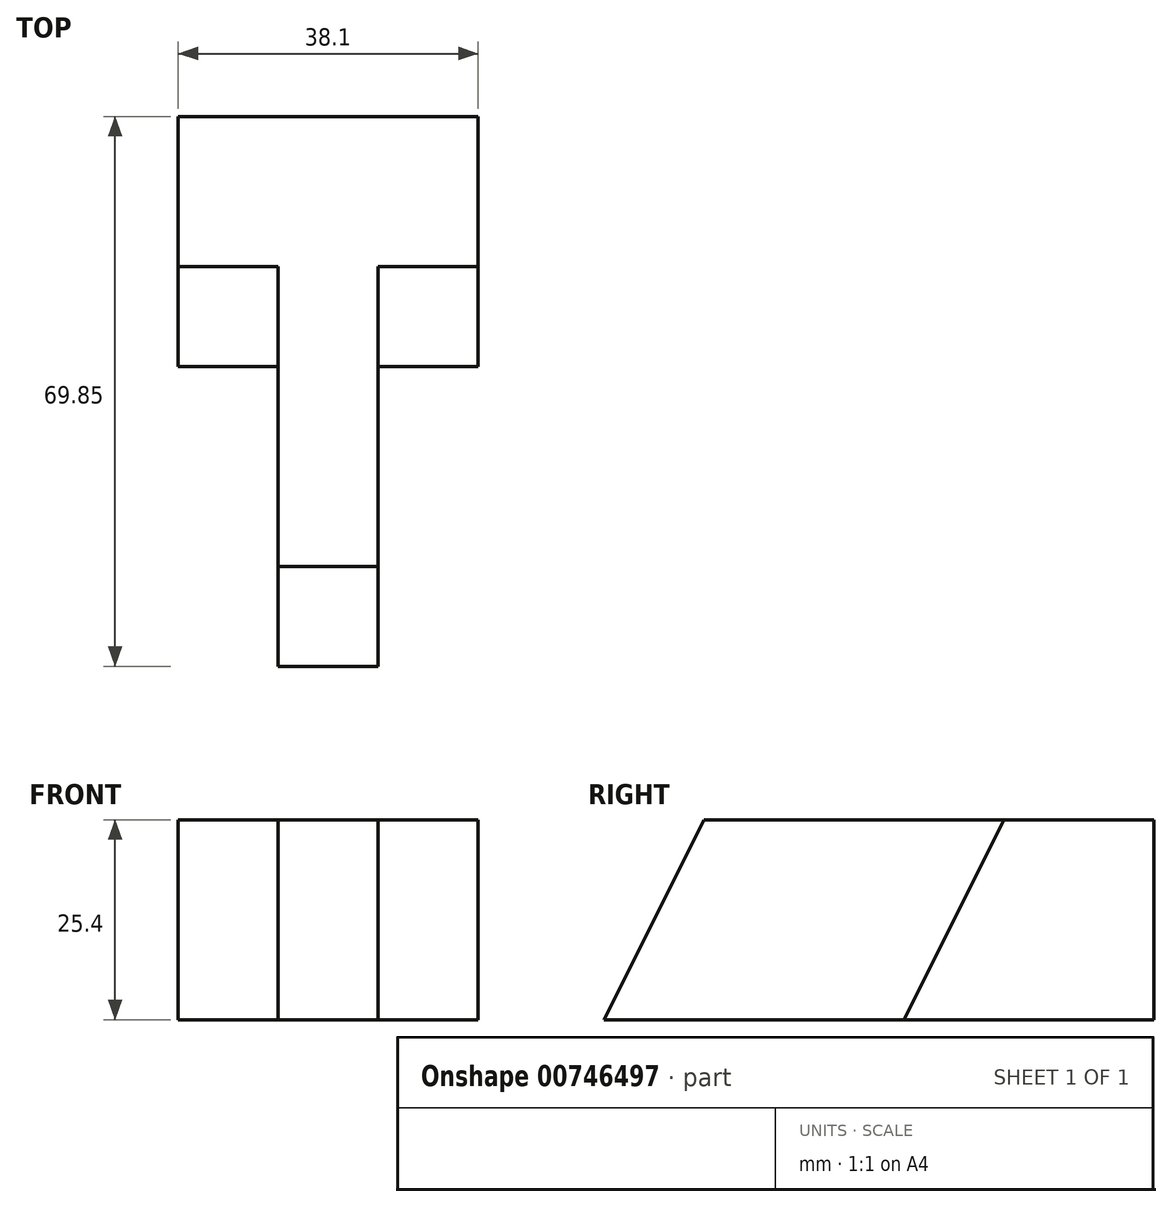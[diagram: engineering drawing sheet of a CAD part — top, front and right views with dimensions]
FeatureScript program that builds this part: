
annotation { "Feature Type Name" : "Feature", "Feature Type Description" : "" }
export const myFeature = defineFeature(function(context is Context, id is Id, definition is map)
    precondition{}
    {
        {
            var Q0;
            Q0=qCreatedBy(makeId("Top.planeOp"),FACE);
            var sketch = newSketch(context, id + "F0", { "sketchPlane" : qUnion([Q0])});
            skLineSegment(sketch, "E0", {"start": v(0, 0) * mm, "end": v(0, 38.1) * mm});
            skLineSegment(sketch, "E1", {"start": v(0, 38.1) * mm, "end": v(-12.7, 38.1) * mm});
            skLineSegment(sketch, "E2", {"start": v(-12.7, 38.1) * mm, "end": v(-12.7, 69.85) * mm});
            skLineSegment(sketch, "E3", {"start": v(-12.7, 69.85) * mm, "end": v(25.4, 69.85) * mm});
            skLineSegment(sketch, "E4", {"start": v(25.4, 69.85) * mm, "end": v(25.4, 38.1) * mm});
            skLineSegment(sketch, "E5", {"start": v(25.4, 38.1) * mm, "end": v(12.7, 38.1) * mm});
            skLineSegment(sketch, "E6", {"start": v(12.7, 38.1) * mm, "end": v(12.7, 0) * mm});
            skLineSegment(sketch, "E7", {"start": v(12.7, 0) * mm, "end": v(0, 0) * mm});
            skSolve(sketch);
        }
        {
            var Q0;
            Q0 = qSketchRegion(id + "F0", true);
            extrude(context, id + "F1", {"entities" : qUnion([Q0]), "depth" : 25.4 * mm, "offsetDistance" : 25.4 * mm});
        }
        {
            var Q0;
            Q0=makeQuery(id+"F1.opExtrude","SWEPT_FACE",FACE,{"disambiguationData":[OSD([sQuery(id+"F0.wireOp",EDGE,"E2")])]});
            var sketch = newSketch(context, id + "F2", { "sketchPlane" : qUnion([Q0])});
            skLineSegment(sketch, "E8", {"start": v(-38.1, 0) * mm, "end": v(-38.1, 25.4) * mm});
            skLineSegment(sketch, "E9", {"start": v(-38.1, 25.4) * mm, "end": v(-50.8, 25.4) * mm});
            skLineSegment(sketch, "E10", {"start": v(-50.8, 25.4) * mm, "end": v(-38.1, 0) * mm});
            skSolve(sketch);
        }
        {
            var Q0;
            Q0=makeQuery(id+"F2.imprint","IMPRINT",FACE,{"disambiguationData":[TD([[makeQuery(id+"F2.imprint","IMPRINT",EDGE,{"derivedFrom":sQuery(id+"F2.wireOp",EDGE,"E8")}),-1.0]])]});
            extrude(context, id + "F3", {"entities" : qUnion([Q0]), "operationType" : NewBodyOperationType.REMOVE, "oppositeDirection" : true, "depth" : 12.7 * mm, "offsetDistance" : 25.4 * mm});
        }
        {
            var Q0;
            Q0=makeQuery(id+"F1.opExtrude","SWEPT_FACE",FACE,{"disambiguationData":[OSD([sQuery(id+"F0.wireOp",EDGE,"E4")])]});
            var sketch = newSketch(context, id + "F4", { "sketchPlane" : qUnion([Q0])});
            skLineSegment(sketch, "E11", {"start": v(38.1, 25.4) * mm, "end": v(50.8, 25.4) * mm});
            skLineSegment(sketch, "E12", {"start": v(50.8, 25.4) * mm, "end": v(38.1, 0) * mm});
            skLineSegment(sketch, "E13", {"start": v(38.1, 0) * mm, "end": v(38.1, 25.4) * mm});
            skSolve(sketch);
        }
        {
            var Q0;
            Q0=makeQuery(id+"F4.imprint","IMPRINT",FACE,{"disambiguationData":[TD([[makeQuery(id+"F4.imprint","IMPRINT",EDGE,{"derivedFrom":sQuery(id+"F4.wireOp",EDGE,"E12")}),-1.0]])]});
            extrude(context, id + "F5", {"entities" : qUnion([Q0]), "operationType" : NewBodyOperationType.REMOVE, "oppositeDirection" : true, "depth" : 12.7 * mm, "offsetDistance" : 25.4 * mm});
        }
        {
            var Q0;
            Q0=makeQuery(id+"F5.boolean.opBoolean","MERGE",FACE,{"derivedFrom":[makeQuery(id+"F1.opExtrude","SWEPT_FACE",FACE,{"disambiguationData":[OSD([sQuery(id+"F0.wireOp",EDGE,"E6")])]}),makeQuery(id+"F5.opExtrude","CAP_FACE",FACE,{"disambiguationData":[OSD([sQuery(id+"F4.wireOp",EDGE,"E12"),sQuery(id+"F4.wireOp",EDGE,"E13"),sQuery(id+"F4.wireOp",EDGE,"E11")])],"isStart":false})]});
            var sketch = newSketch(context, id + "F6", { "sketchPlane" : qUnion([Q0])});
            skLineSegment(sketch, "E14", {"start": v(0, 25.4) * mm, "end": v(12.7, 25.4) * mm});
            skLineSegment(sketch, "E15", {"start": v(12.7, 25.4) * mm, "end": v(0, 0) * mm});
            skLineSegment(sketch, "E16", {"start": v(0, 0) * mm, "end": v(0, 25.4) * mm});
            skSolve(sketch);
        }
        {
            var Q0;
            Q0=makeQuery(id+"F6.imprint","IMPRINT",FACE,{"disambiguationData":[TD([[makeQuery(id+"F6.imprint","IMPRINT",EDGE,{"derivedFrom":sQuery(id+"F6.wireOp",EDGE,"E14")}),1.0]])]});
            extrude(context, id + "F7", {"entities" : qUnion([Q0]), "operationType" : NewBodyOperationType.REMOVE, "oppositeDirection" : true, "depth" : 12.7 * mm, "offsetDistance" : 25.4 * mm});
        }
    });
